# Revit family: LEGRAND_PRISES_NON_VERROUILLEES_ENCASTREES_IP44_230
name_source: partatom
category: Installations électriques
revit_build: Autodesk Revit 2018 (Build: 20170223_1515(x64)
units: mm (PartAtom-declared; Revit-internal decimal feet)

## family parameters
Conserver l'orientation des annotations = Non
Cote de connecteur circulaire = Utiliser le diamètre
Couper avec des vides une fois chargée = Non
Hôte = Face
Partagée = Non
Point de calcul de pièce = Non
Type d'élément = Normal

## types (17) — shared parameters
Conditions Générale d'Utilisation = https://export.legrand.com
Couleur caractéristique = bleu
Description = Prise au standard international pour montage encastré ou saillie avec accessoire permet la connexion d'appareils de puissance
Elévation par défaut = 1000 mm
Fabricant = Legrand
Température maximale d'installation = 40°C
Température maximum d'utilisation = 100°C
Température minimum d'installation = -20°C
Température minimum d'utilisation = -50°C
Tension V = 230 V  50/60 Hz  bleu
classe de protection IP = IP44
installation Encastrée E ou Saillie S = encastré et saillie
type de raccordement = bornes à vis

## per-type parameters (varying)
| type | Dia bouchon | Intensité A | Modèle | Nombre de pôles | Position de la Terre h | RAY BOUCHON | Ray | Standard CEI ou NFC | entraxe de fixation horizontal mm | entraxe de fixation vertical mm | h1 | hauteur mm | largeur mm | matériau du boitier | profondeur d'encastrement mm | profondeur mm | résistance aux chocs IK | sans halogène |
| Socle tableau à entraxe unifié Hypra   IP44   16 A   200/250 V   2P+T | 55 mm | 16 A | 052018 | 3 | 6 | 27 mm | 27 mm | CEI | 70 mm | 70 mm | 50 mm | 84 mm | 84 mm | plastique | 37 mm | 73 mm  [stored 0.239501 ft] | 09 | Oui |
| Socle tableau à entraxe unifié Hypra   IP44   16 A   200/250 V   3P+T | 55 mm | 16 A | 052019 | 4 | 9 | 27 mm | 27 mm | CEI | 70 mm | 70 mm | 50 mm | 84 mm | 84 mm | plastique | 43 mm | 84 mm | 09 | Oui |
| Socle tableau à entraxe unifié Hypra   IP44   16 A   200/250 V  3P+N+T | 55 mm | 16 A | 052020 | 5 | 9 | 27 mm | 27 mm | CEI | 70 mm | 70 mm | 50 mm | 84 mm | 84 mm | plastique | 43 mm | 80 mm | 09 | Oui |
| Socle tableau Hypra   IP44   16 A   200/250 V   2P+T   plast | 42 mm | 16 A | 052022 | 3 | 6 | 21 mm  [stored 0.0688976 ft] | 21 mm  [stored 0.0688976 ft] | CEI | 52 mm | 60 mm | 43 mm | 72 mm | 64 mm | plastique | 41 mm | 81 mm | 09 | Oui |
| Socle tableau Hypra   IP44   16 A   200/250 V   3P+T   plast | 48 mm | 16 A | 052023 | 4 | 9 | 24 mm | 24 mm | CEI | 60 mm | 70 mm | 50 mm | 84 mm | 74 mm | plastique | 44 mm | 84 mm | 09 | Oui |
| Socle tableau Hypra   IP44   16 A   200/250 V   3P+N+T   plast | 48 mm | 16 A | 052024 | 5 | 9 | 24 mm | 24 mm | CEI | 60 mm | 70 mm | 50 mm | 84 mm | 74 mm | plastique | 44 mm | 88 mm | 09 | Oui |
| Socle de tableau Hypra   IP44   16 A   200/250 V   2P+T   métal | 42 mm | 16 A | 052032 | 3 | 6 | 21 mm  [stored 0.0688976 ft] | 21 mm  [stored 0.0688976 ft] | CEI | 52 mm | 60 mm | 43 mm | 72 mm | 64 mm | métal | 41 mm | 81 mm | 10 | Oui |
| Socle de tableau Hypra   IP44   16 A   200/250 V   3P+N+T   métal | 48 mm | 16 A | 052034 | 5 | 9 | 24 mm | 24 mm | CEI | 60 mm | 70 mm | 50 mm | 84 mm | 74 mm | métal | 44 mm | 88 mm | 10 | Oui |
| Socle tableau Hypra   IP44   32 A   200/250 V   2P+T   plast | 55 mm | 32 A | 052718 | 3 | 6 | 27 mm | 27 mm | CEI | 70 mm | 70 mm | 56 mm | 94 mm | 84 mm | plastique | 50 mm | 103 mm | 09 | Oui |
| Socle tableau Hypra   IP44   32 A   200/250 V   3P+T   plast | 55 mm | 32 A | 052719 | 4 | 9 | 27 mm | 27 mm | CEI | 70 mm | 70 mm | 56 mm | 94 mm | 84 mm | plastique | 50 mm | 103 mm | 09 | Oui |
| Socle tableau Hypra   IP44   32 A   200/250 V   3P+N+T   plast | 55 mm | 32 A | 052720 | 5 | 9 | 27 mm | 27 mm | CEI | 70 mm | 70 mm | 50 mm | 84 mm | 84 mm | plastique | 52 mm | 108 mm | 09 | Oui |
| Socle tableau Hypra   IP44   32 A   200/250 V   2P+T   métal | 55 mm | 32 A | 052732 | 5 | 9 | 27 mm | 27 mm | CEI | 70 mm | 80 mm | 56 mm | 94 mm | 84 mm | métal | 50 mm | 103 mm | 09 | Oui |
| Socle tableau Hypra   IP44   32 A   200/250 V   3P+T   métal | 55 mm | 32 A | 052733 | 4 | 9 | 27 mm | 27 mm | CEI | 70 mm | 80 mm | 56 mm | 94 mm | 84 mm | métal | 50 mm | 103 mm | 10 | Oui |
| Socle tableau Hypra   IP44   63 A   200/250 V   2P+T   plast | 95 mm | 63 A | 053622 | 3 | 6 | 47 mm | 47 mm | CEI | 77 mm | 85 mm | 88 mm | 146 mm  [stored 0.479003 ft] | 146 mm  [stored 0.479003 ft] | plastique | 98 mm | 168 mm | 09 | Non |
| Socle tableau Hypra   IP44   63 A   200/250 V   3P+T   plast | 69 mm | 63 A | 053623 | 4 | 9 | 34 mm | 34 mm | CEI | 77 mm | 85 mm | 64 mm | 106 mm | 106 mm | plastique | 98 mm | 168 mm | 09 | Non |
| Socle tableau Hypra   IP44   16 A   250 v   2P+T   brochage domestique plast | 44 mm | 16 A | 053903 | 3 | 6 | 22 mm | 22 mm | NFC | 55 mm | 55 mm | 40 mm | 67 mm | 67 mm | plastique | 19 mm | 49 mm | 09 | Oui |
| Socle de tableau Hypra   IP44   16 A   200/250 V   3P+T   métal | 48 mm | 16 A | 052033 | 4 | 9 | 24 mm | 24 mm | CEI | 60 mm | 70 mm | 50 mm | 84 mm | 74 mm | métal | 44 mm | 84 mm | 10 | Oui |

note: [stored X ft] marks values corroborated as IEEE doubles in the binary element streams (Revit-internal decimal feet)
